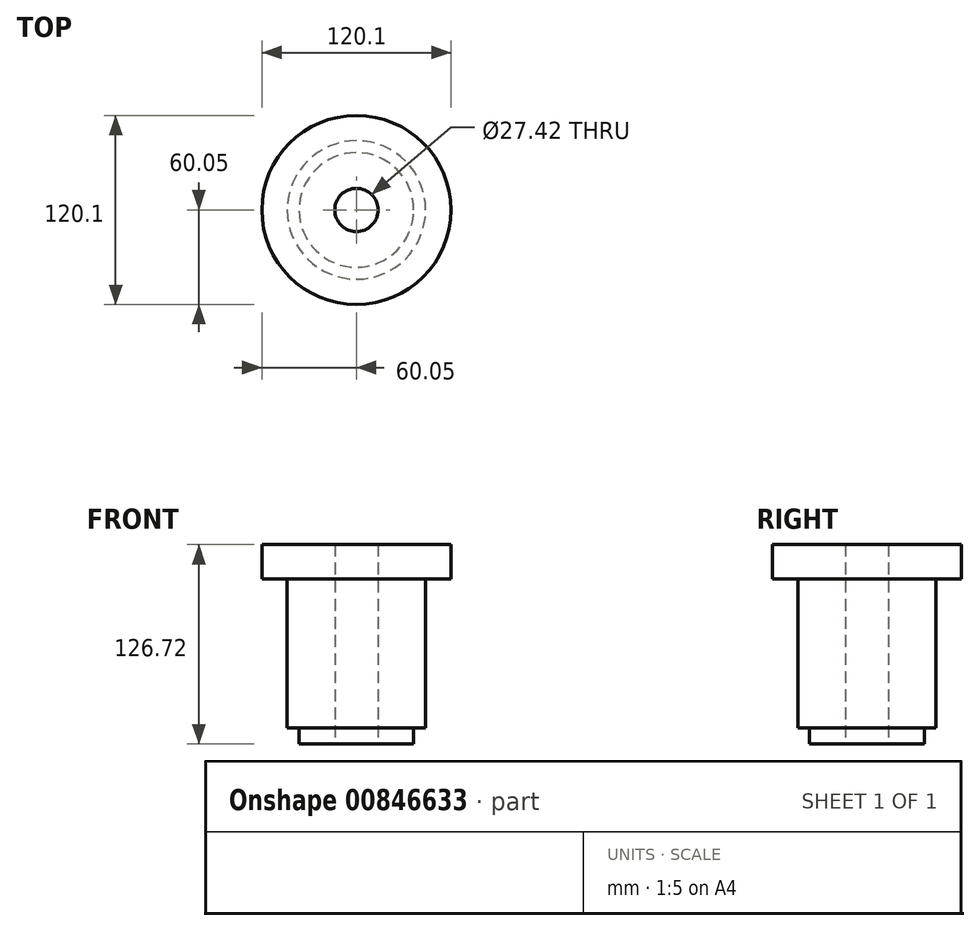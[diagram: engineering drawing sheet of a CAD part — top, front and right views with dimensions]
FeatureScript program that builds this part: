
annotation { "Feature Type Name" : "Feature", "Feature Type Description" : "" }
export const myFeature = defineFeature(function(context is Context, id is Id, definition is map)
    precondition{}
    {
        {
            var Q0;
            Q0=qCreatedBy(makeId("Front.planeOp"),FACE);
            var sketch = newSketch(context, id + "F0", { "sketchPlane" : qUnion([Q0])});
            skLineSegment(sketch, "E0", {"start": v(0, 2) * mm, "end": v(0, 117.1) * mm, "construction": true});
            skLineSegment(sketch, "E1", {"start": v(-13.71, -25.48) * mm, "end": v(-13.71, 101.24) * mm});
            skLineSegment(sketch, "E2", {"start": v(-13.71, 101.24) * mm, "end": v(-60.05, 101.24) * mm});
            skLineSegment(sketch, "E3", {"start": v(-60.05, 101.24) * mm, "end": v(-60.05, 79.46) * mm});
            skLineSegment(sketch, "E4", {"start": v(-60.05, 79.46) * mm, "end": v(-43.97, 79.46) * mm});
            skLineSegment(sketch, "E5", {"start": v(-43.97, 79.46) * mm, "end": v(-43.97, -15.06) * mm});
            skLineSegment(sketch, "E6", {"start": v(-43.97, -15.06) * mm, "end": v(-36.4, -15.06) * mm});
            skLineSegment(sketch, "E7", {"start": v(-36.4, -15.06) * mm, "end": v(-36.4, -25.48) * mm});
            skLineSegment(sketch, "E8", {"start": v(-36.4, -25.48) * mm, "end": v(-13.71, -25.48) * mm});
            skSolve(sketch);
        }
        {
            var Q0;
            Q0=makeQuery(id+"F0.imprint","IMPRINT",FACE,{"disambiguationData":[TD([[makeQuery(id+"F0.imprint","IMPRINT",EDGE,{"derivedFrom":sQuery(id+"F0.wireOp",EDGE,"E1")}),1.0]])]});
            var Q1;
            Q1=sQuery(id+"F0.wireOp",EDGE,"E0");
            revolve(context, id + "F1", {"surfaceOperationType" : NewSurfaceOperationType.NEW, "entities" : qUnion([Q0]), "axis" : qUnion([Q1]), "revolveType" : RevolveType.FULL});
        }
    });
